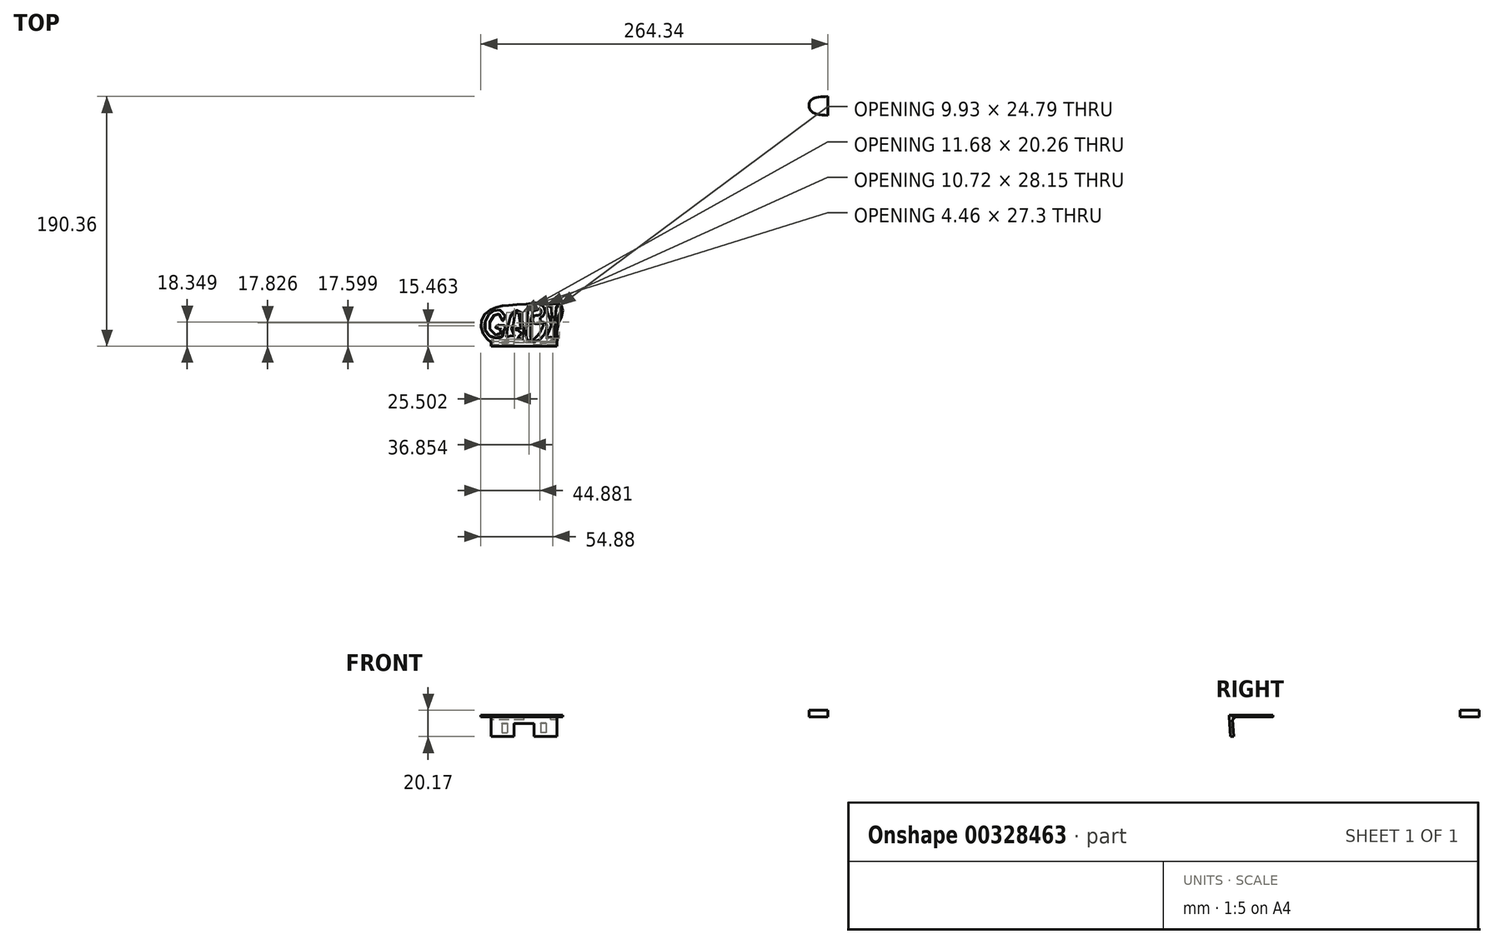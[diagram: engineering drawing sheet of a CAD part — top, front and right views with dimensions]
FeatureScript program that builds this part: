
annotation { "Feature Type Name" : "Feature", "Feature Type Description" : "" }
export const myFeature = defineFeature(function(context is Context, id is Id, definition is map)
    precondition{}
    {
        {
            var Q0;
            Q0=qCreatedBy(makeId("Top.planeOp"),FACE);
            var sketch = newSketch(context, id + "F0", { "sketchPlane" : qUnion([Q0])});
            skFitSpline(sketch, "E0", {"points": [v(208.46, 258.66) * mm, v(204.58, 269.31) * mm, v(190.2, 270.84) * mm, v(170.66, 244.78) * mm, v(175.88, 214.28) * mm, v(202.96, 201.63) * mm, v(209.26, 221.43) * mm, v(194.86, 220.98) * mm, v(190.41, 232.54) * mm, v(207.55, 235.55) * mm, v(222.9, 231.9) * mm, v(223.35, 220.5) * mm, v(217.5, 219.9) * mm, v(214.97, 200.91) * mm, v(194.5, 191.92) * mm, v(169.76, 199.8) * mm, v(153.7, 227.32) * mm, v(164.47, 265.69) * mm, v(182.9, 280.99) * mm, v(205.7, 283.65) * mm, v(222.26, 256.23) * mm, v(210.9, 248.92) * mm, v(208.46, 258.66) * mm]});
            skFitSpline(sketch, "E1", {"points": [v(226.73, 195.08) * mm, v(238.3, 258.75) * mm, v(248.5, 277.8) * mm, v(255.75, 283.53) * mm, v(275.96, 276.82) * mm, v(277.46, 252.22) * mm, v(280.5, 190.57) * mm, v(263.52, 190.56) * mm, v(275.95, 207.94) * mm, v(270.28, 216) * mm, v(247.52, 220.67) * mm, v(248.95, 226.5) * mm, v(271.39, 220.1) * mm, v(270.46, 246.7) * mm, v(264.68, 277.8) * mm, v(255.46, 275.75) * mm, v(250.85, 253.79) * mm, v(251.04, 240.44) * mm, v(242.53, 224.24) * mm, v(252.29, 195.78) * mm, v(236.68, 199.8) * mm, v(226.73, 195.08) * mm]});
            skFitSpline(sketch, "E2", {"points": [v(292.24, 193.17) * mm, v(296.68, 287.3) * mm, v(299.21, 300.98) * mm, v(309.7, 302.35) * mm, v(307.43, 294.14) * mm, v(311.54, 279.98) * mm, v(306.51, 245.3) * mm, v(304.8, 215.23) * mm, v(306.66, 192.3) * mm, v(315.66, 187.45) * mm, v(346.65, 237.97) * mm, v(316.69, 241) * mm, v(317.94, 265.42) * mm, v(332.95, 267.2) * mm, v(341.51, 280.98) * mm, v(330.75, 288.2) * mm, v(318.05, 281.85) * mm, v(315.11, 300.43) * mm, v(334.83, 304.63) * mm, v(352.27, 287.6) * mm, v(343.37, 261.57) * mm, v(319.58, 256.67) * mm, v(320.91, 246.6) * mm, v(356.91, 240.4) * mm, v(336.82, 187.5) * mm, v(300.36, 183.9) * mm, v(292.24, 193.17) * mm]});
            skLineSegment(sketch, "E3", {"start": v(307, 191.46) * mm, "end": v(307.14, 182.1) * mm});
            skLineSegment(sketch, "E4", {"start": v(313.38, 181.25) * mm, "end": v(313.3, 186.71) * mm});
            skLineSegment(sketch, "E5", {"start": v(332.02, 238.03) * mm, "end": v(332.02, 265.36) * mm});
            skLineSegment(sketch, "E6", {"start": v(337.72, 265.76) * mm, "end": v(337.72, 238.33) * mm});
            skFitSpline(sketch, "E7", {"points": [v(358.27, 294.6) * mm, v(373.81, 243.63) * mm, v(364.41, 210) * mm, v(359.35, 190.49) * mm, v(373.81, 194.83) * mm, v(384.66, 190.49) * mm, v(383.2, 211.46) * mm, v(402, 273.27) * mm, v(404.54, 296.77) * mm, v(393.33, 297.49) * mm, v(389.35, 271.46) * mm, v(381.76, 247.97) * mm, v(376.34, 271.46) * mm, v(370.2, 298.21) * mm, v(358.27, 294.6) * mm]});
            skFitSpline(sketch, "E8", {"points": [v(312.21, 307.06) * mm, v(238.94, 301.07) * mm, v(198.48, 295.37) * mm, v(159.35, 276.06) * mm, v(141.26, 235.1) * mm, v(159.53, 191.03) * mm, v(178.15, 176.56) * mm, v(183.3, 176.56) * mm, v(194.48, 176.56) * mm, v(219.49, 176.56) * mm, v(261.86, 176.56) * mm, v(309.55, 176.56) * mm, v(332.54, 176.56) * mm, v(342.1, 176.56) * mm, v(383.86, 176.56) * mm, v(394.64, 176.56) * mm, v(394.63, 228.25) * mm, v(412.34, 273.8) * mm, v(404.4, 303.08) * mm, v(375.47, 304.53) * mm, v(339.33, 310.31) * mm, v(312.21, 307.06) * mm]});
            skLineSegment(sketch, "E9.bottom", {"start": v(1325.4, 499.43) * mm, "end": v(1425.4, 499.43) * mm});
            skLineSegment(sketch, "E9.top", {"start": v(1325.4, 399.43) * mm, "end": v(1425.4, 399.43) * mm});
            skLineSegment(sketch, "E9.left", {"start": v(1325.4, 499.43) * mm, "end": v(1325.4, 399.43) * mm});
            skLineSegment(sketch, "E9.right", {"start": v(1425.4, 499.43) * mm, "end": v(1425.4, 399.43) * mm});
            skLineSegment(sketch, "E10", {"start": v(144.45, 176.56) * mm, "end": v(455.26, 176.56) * mm, "construction": true});
            skSolve(sketch);
        }
        {
            var Q0;
            Q0=makeQuery(id+"F0.imprint","IMPRINT",FACE,{"disambiguationData":[TD([[makeQuery(id+"F0.imprint","IMPRINT",EDGE,{"derivedFrom":sQuery(id+"F0.wireOp",EDGE,"E0")}),1.0]])]});
            var Q1;
            {var subQ0=sQuery(id+"F0.wireOp",EDGE,"E5");var subQ1=sQuery(id+"F0.wireOp",EDGE,"E2");var subQ2=makeQuery(id+"F0.imprint","INTERSECT",VERTEX,{"disambiguationData":[OD(2.0)],"derivedFrom":[subQ1,subQ0]});Q1=makeQuery(id+"F0.imprint","IMPRINT",FACE,{"disambiguationData":[TD([[makeQuery(id+"F0.imprint","IMPRINT",EDGE,{"disambiguationData":[TD([[subQ2,-1.0]])],"derivedFrom":subQ1}),1.0]])]});}
            var Q2;
            {var subQ0=sQuery(id+"F0.wireOp",EDGE,"E6");var subQ1=sQuery(id+"F0.wireOp",EDGE,"E2");var subQ2=makeQuery(id+"F0.imprint","INTERSECT",VERTEX,{"disambiguationData":[OD(2.0)],"derivedFrom":[subQ1,subQ0]});Q2=makeQuery(id+"F0.imprint","IMPRINT",FACE,{"disambiguationData":[TD([[makeQuery(id+"F0.imprint","IMPRINT",EDGE,{"disambiguationData":[TD([[subQ2,-1.0]])],"derivedFrom":subQ1}),1.0]])]});}
            var Q3;
            {var subQ0=sQuery(id+"F0.wireOp",EDGE,"E5");var subQ1=sQuery(id+"F0.wireOp",EDGE,"E2");var subQ2=makeQuery(id+"F0.imprint","INTERSECT",VERTEX,{"disambiguationData":[OD(1.0)],"derivedFrom":[subQ1,subQ0]});Q3=makeQuery(id+"F0.imprint","IMPRINT",FACE,{"disambiguationData":[TD([[makeQuery(id+"F0.imprint","IMPRINT",EDGE,{"disambiguationData":[TD([[subQ2,-1.0]])],"derivedFrom":subQ1}),1.0]])]});}
            var Q4;
            {var subQ0=sQuery(id+"F0.wireOp",EDGE,"E3");Q4=makeQuery(id+"F0.imprint","IMPRINT",FACE,{"disambiguationData":[TD([[makeQuery(id+"F0.imprint","IMPRINT",EDGE,{"derivedFrom":subQ0}),1.0]])]});}
            extrude(context, id + "F1", {"entities" : qUnion([Q0, Q1, Q2, Q3, Q4]), "depth" : 5 * mm});
        }
        {
            var Q0;
            Q0=qCreatedBy(makeId("Top.planeOp"),FACE);
            var sketch = newSketch(context, id + "F2", { "sketchPlane" : qUnion([Q0])});
            skPoint(sketch, "E11", {"position": v(45.7, 40) * mm});
            skLineSegment(sketch, "E12.bottom", {"start": v(45.7, 40) * mm, "end": v(105.7, 40) * mm});
            skLineSegment(sketch, "E12.top", {"start": v(45.7, 100) * mm, "end": v(105.7, 100) * mm});
            skLineSegment(sketch, "E12.left", {"start": v(45.7, 40) * mm, "end": v(45.7, 100) * mm});
            skLineSegment(sketch, "E12.right", {"start": v(105.7, 40) * mm, "end": v(105.7, 100) * mm});
            skSolve(sketch);
        }
        {
            var Q0;
            Q0=makeQuery(id+"F1.opExtrude","SWEPT_BODY",BODY,{"disambiguationData":[OSD([sQuery(id+"F0.wireOp",EDGE,"E0"),sQuery(id+"F0.wireOp",EDGE,"E1"),sQuery(id+"F0.wireOp",EDGE,"E2"),sQuery(id+"F0.wireOp",EDGE,"E3"),sQuery(id+"F0.wireOp",EDGE,"E4"),sQuery(id+"F0.wireOp",EDGE,"E7"),sQuery(id+"F0.wireOp",EDGE,"E8")])]});
            var Q1;
            Q1=sQuery(id+"F2.wireOp",VERTEX,"E11");
            transform(context, id + "F3", {"entities" : qUnion([Q0]), "transformType" : TransformType.SCALE_UNIFORMLY, "scale" : 0.23, "scalePoint" : qUnion([Q1]), "makeCopy" : false});
        }
        {
            var Q0;
            Q0=qCreatedBy(makeId("Top.planeOp"),FACE);
            var sketch = newSketch(context, id + "F4", { "sketchPlane" : qUnion([Q0])});
            skLineSegment(sketch, "E13.bottom", {"start": v(64.57, 106.66) * mm, "end": v(137.5, 106.66) * mm});
            skLineSegment(sketch, "E13.top", {"start": v(64.57, 65.78) * mm, "end": v(137.5, 65.78) * mm});
            skLineSegment(sketch, "E13.left", {"start": v(64.57, 106.66) * mm, "end": v(64.57, 65.78) * mm});
            skLineSegment(sketch, "E13.right", {"start": v(137.5, 106.66) * mm, "end": v(137.5, 65.78) * mm});
            skLineSegment(sketch, "E14.bottom", {"start": v(75.61, 71.73) * mm, "end": v(125.61, 71.73) * mm});
            skLineSegment(sketch, "E14.top", {"start": v(75.61, 68.73) * mm, "end": v(125.61, 68.73) * mm});
            skLineSegment(sketch, "E14.left", {"start": v(75.61, 71.73) * mm, "end": v(75.61, 68.73) * mm});
            skLineSegment(sketch, "E14.right", {"start": v(125.61, 71.73) * mm, "end": v(125.61, 68.73) * mm});
            skSolve(sketch);
        }
        {
            var Q0;
            Q0=makeQuery(id+"F4.imprint","IMPRINT",FACE,{"disambiguationData":[TD([[makeQuery(id+"F4.imprint","IMPRINT",EDGE,{"derivedFrom":sQuery(id+"F4.wireOp",EDGE,"E14.bottom")}),-1.0]])]});
            var Q1;
            Q1=makeQuery(id+"F1.opExtrude","CAP_FACE",FACE,{"disambiguationData":[OSD([sQuery(id+"F0.wireOp",EDGE,"E0"),sQuery(id+"F0.wireOp",EDGE,"E1"),sQuery(id+"F0.wireOp",EDGE,"E2"),sQuery(id+"F0.wireOp",EDGE,"E3"),sQuery(id+"F0.wireOp",EDGE,"E4"),sQuery(id+"F0.wireOp",EDGE,"E7"),sQuery(id+"F0.wireOp",EDGE,"E8")])],"isStart":false});
            extrude(context, id + "F5", {"entities" : qUnion([Q0]), "operationType" : NewBodyOperationType.ADD, "endBound" : BoundingType.UP_TO_SURFACE, "endBoundEntityFace" : qUnion([Q1]), "depth" : 2 * mm});
        }
        {
            var Q0;
            Q0=makeQuery(id+"F5.opExtrude","SWEPT_FACE",FACE,{"disambiguationData":[OSD([sQuery(id+"F4.wireOp",EDGE,"E14.left")])]});
            var sketch = newSketch(context, id + "F6", { "sketchPlane" : qUnion([Q0])});
            skLineSegment(sketch, "E15", {"start": v(-68.73, 0) * mm, "end": v(-69.79, -15.17) * mm});
            skLineSegment(sketch, "E16", {"start": v(-69.79, -15.17) * mm, "end": v(-72.27, -15) * mm});
            skLineSegment(sketch, "E17", {"start": v(-72.27, -15) * mm, "end": v(-71.22, 0) * mm});
            skLineSegment(sketch, "E18", {"start": v(-66.94, 0) * mm, "end": v(-59.6, 0) * mm, "construction": true});
            skLineSegment(sketch, "E19", {"start": v(-68.73, 0) * mm, "end": v(-68.73, 1.15) * mm});
            skLineSegment(sketch, "E20", {"start": v(-68.73, 1.15) * mm, "end": v(-71.22, 0) * mm});
            skLineSegment(sketch, "E21", {"start": v(-71.39, -2.42) * mm, "end": v(-73.34, 0) * mm});
            skLineSegment(sketch, "E22", {"start": v(-73.34, 0) * mm, "end": v(-71.22, 0) * mm});
            skSolve(sketch);
        }
        {
            var Q0;
            {var subQ0=sQuery(id+"F6.wireOp",EDGE,"E16");Q0=makeQuery(id+"F6.imprint","IMPRINT",FACE,{"disambiguationData":[TD([[makeQuery(id+"F6.imprint","IMPRINT",EDGE,{"derivedFrom":subQ0}),-1.0]])]});}
            var Q1;
            Q1=makeQuery(id+"F5.opExtrude","CAP_VERTEX",VERTEX,{"disambiguationData":[OSD([sQuery(id+"F4.wireOp",EDGE,"E14.top"),sQuery(id+"F4.wireOp",EDGE,"E14.right")])],"isStart":true});
            extrude(context, id + "F7", {"entities" : qUnion([Q0]), "operationType" : NewBodyOperationType.ADD, "endBound" : BoundingType.UP_TO_VERTEX, "oppositeDirection" : true, "endBoundEntityVertex" : qUnion([Q1]), "depth" : 25 * mm});
        }
        {
            var Q0;
            Q0=makeQuery(id+"F7.opExtrude","SWEPT_FACE",FACE,{"disambiguationData":[OSD([sQuery(id+"F6.wireOp",EDGE,"E17")])]});
            var sketch = newSketch(context, id + "F8", { "sketchPlane" : qUnion([Q0])});
            skLineSegment(sketch, "E23.bottom", {"start": v(-117.41, -9.97) * mm, "end": v(-113.41, -9.97) * mm});
            skLineSegment(sketch, "E23.top", {"start": v(-117.41, -17) * mm, "end": v(-113.41, -17) * mm});
            skLineSegment(sketch, "E23.left", {"start": v(-117.41, -9.97) * mm, "end": v(-117.41, -17) * mm});
            skLineSegment(sketch, "E23.right", {"start": v(-113.41, -9.97) * mm, "end": v(-113.41, -17) * mm});
            skLineSegment(sketch, "E24", {"start": v(-100.61, -40.03) * mm, "end": v(-100.61, -55.9) * mm});
            skPoint(sketch, "E24.startSnap0", {"position": v(-100.61, -20) * mm});
            skLineSegment(sketch, "E25.MirrorCS", {"start": v(-87.81, -9.97) * mm, "end": v(-87.81, -17) * mm});
            skLineSegment(sketch, "E26.MirrorCS", {"start": v(-83.81, -9.97) * mm, "end": v(-87.81, -9.97) * mm});
            skLineSegment(sketch, "E27.MirrorCS", {"start": v(-83.81, -9.97) * mm, "end": v(-83.81, -17) * mm});
            skLineSegment(sketch, "E28.MirrorCS", {"start": v(-83.81, -17) * mm, "end": v(-87.81, -17) * mm});
            skLineSegment(sketch, "E29.bottom", {"start": v(-108.31, -20) * mm, "end": v(-92.92, -20) * mm});
            skLineSegment(sketch, "E29.top", {"start": v(-108.31, -9.97) * mm, "end": v(-92.92, -9.97) * mm});
            skLineSegment(sketch, "E29.left", {"start": v(-108.31, -20) * mm, "end": v(-108.31, -9.97) * mm});
            skLineSegment(sketch, "E29.right", {"start": v(-92.92, -20) * mm, "end": v(-92.92, -9.97) * mm});
            skPoint(sketch, "E29.middle", {"position": v(-100.61, -14.99) * mm});
            skSolve(sketch);
        }
        {
            var Q0;
            Q0=makeQuery(id+"F8.imprint","IMPRINT",FACE,{"disambiguationData":[TD([[makeQuery(id+"F8.imprint","IMPRINT",EDGE,{"derivedFrom":sQuery(id+"F8.wireOp",EDGE,"E23.bottom")}),-1.0]])]});
            var Q1;
            Q1=makeQuery(id+"F8.imprint","IMPRINT",FACE,{"disambiguationData":[TD([[makeQuery(id+"F8.imprint","IMPRINT",EDGE,{"derivedFrom":sQuery(id+"F8.wireOp",EDGE,"E25.MirrorCS")}),1.0]])]});
            extrude(context, id + "F9", {"entities" : qUnion([Q0, Q1]), "operationType" : NewBodyOperationType.REMOVE, "oppositeDirection" : true, "depth" : 1 * mm});
        }
        {
            var Q0;
            Q0=makeQuery(id+"F8.imprint","IMPRINT",FACE,{"disambiguationData":[TD([[makeQuery(id+"F8.imprint","IMPRINT",EDGE,{"derivedFrom":sQuery(id+"F8.wireOp",EDGE,"E29.bottom")}),1.0]])]});
            extrude(context, id + "F10", {"entities" : qUnion([Q0]), "operationType" : NewBodyOperationType.REMOVE, "oppositeDirection" : true, "depth" : 25 * mm});
        }
        {
            var Q0;
            {var subQ3=sQuery(id+"F6.wireOp",EDGE,"E21");Q0=makeQuery(id+"F6.imprint","IMPRINT",FACE,{"disambiguationData":[TD([[makeQuery(id+"F6.imprint","IMPRINT",EDGE,{"derivedFrom":subQ3}),-1.0]])]});}
            extrude(context, id + "F11", {"entities" : qUnion([Q0]), "operationType" : NewBodyOperationType.ADD, "oppositeDirection" : true, "depth" : 25 * mm});
        }
        {
            var Q0;
            {var subQ3=sQuery(id+"F6.wireOp",EDGE,"E21");Q0=makeQuery(id+"F6.imprint","IMPRINT",FACE,{"disambiguationData":[TD([[makeQuery(id+"F6.imprint","IMPRINT",EDGE,{"derivedFrom":subQ3}),-1.0]])]});}
            var Q1;
            Q1=makeQuery(id+"F7.opExtrude","CAP_VERTEX",VERTEX,{"disambiguationData":[OSD([sQuery(id+"F4.wireOp",EDGE,"E14.left"),sQuery(id+"F6.wireOp",EDGE,"E17")])],"isStart":false});
            extrude(context, id + "F12", {"entities" : qUnion([Q0]), "operationType" : NewBodyOperationType.ADD, "endBound" : BoundingType.UP_TO_VERTEX, "oppositeDirection" : true, "endBoundEntityVertex" : qUnion([Q1]), "depth" : 25 * mm, "hasSecondDirection" : true, "secondDirectionOppositeDirection" : true, "secondDirectionDepth" : 45.3 * mm});
        }
    });
